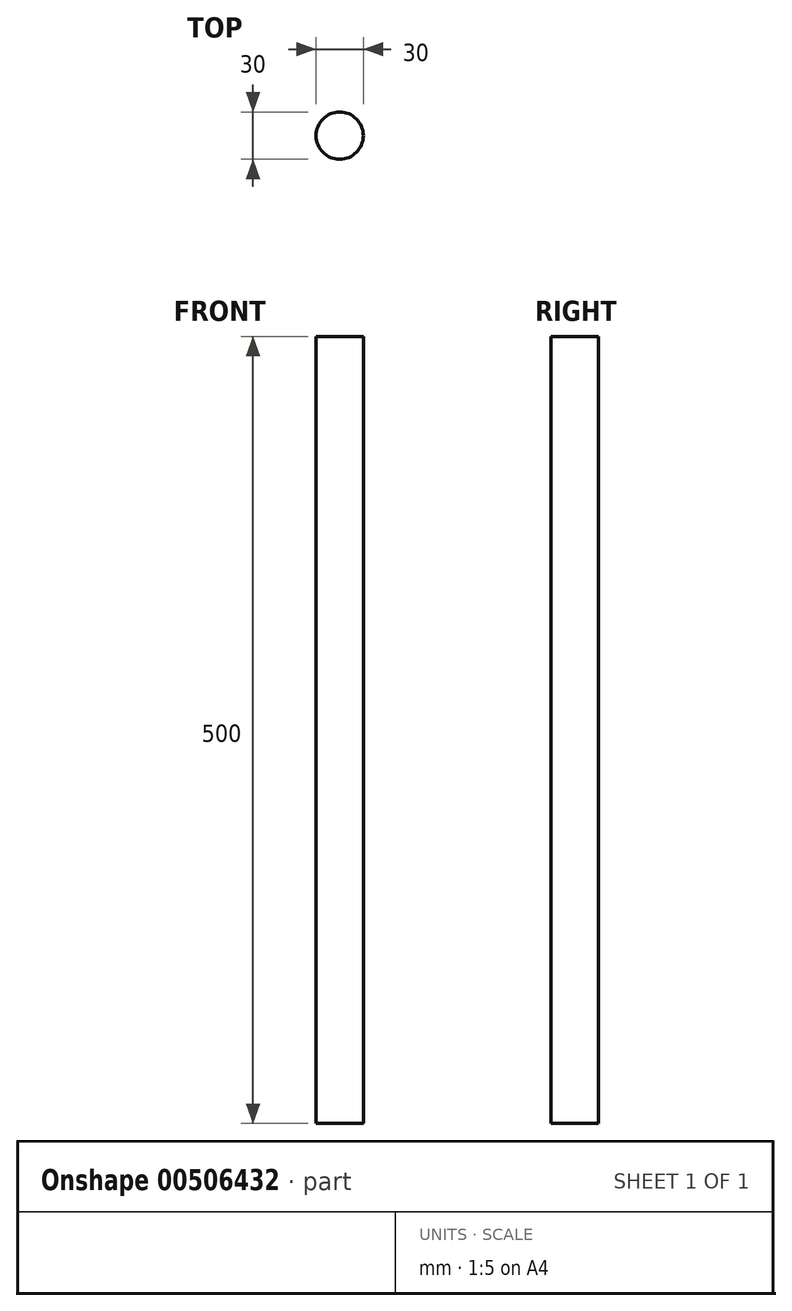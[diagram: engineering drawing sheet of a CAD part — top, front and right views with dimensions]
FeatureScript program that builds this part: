
annotation { "Feature Type Name" : "Feature", "Feature Type Description" : "" }
export const myFeature = defineFeature(function(context is Context, id is Id, definition is map)
    precondition{}
    {
        {
            var Q0;
            Q0=qCreatedBy(makeId("Top.planeOp"),FACE);
            var sketch = newSketch(context, id + "F0", { "sketchPlane" : qUnion([Q0])});
            skCircle(sketch, "E0", {"center": v(0, 0) * mm, "radius": 15 * mm});
            skSolve(sketch);
        }
        {
            var Q0;
            Q0=makeQuery(id+"F0.imprint","IMPRINT",FACE,{"disambiguationData":[TD([[makeQuery(id+"F0.imprint","IMPRINT",EDGE,{"derivedFrom":sQuery(id+"F0.wireOp",EDGE,"E0")}),1.0]])]});
            extrude(context, id + "F1", {"entities" : qUnion([Q0]), "depth" : 500 * mm});
        }
    });
